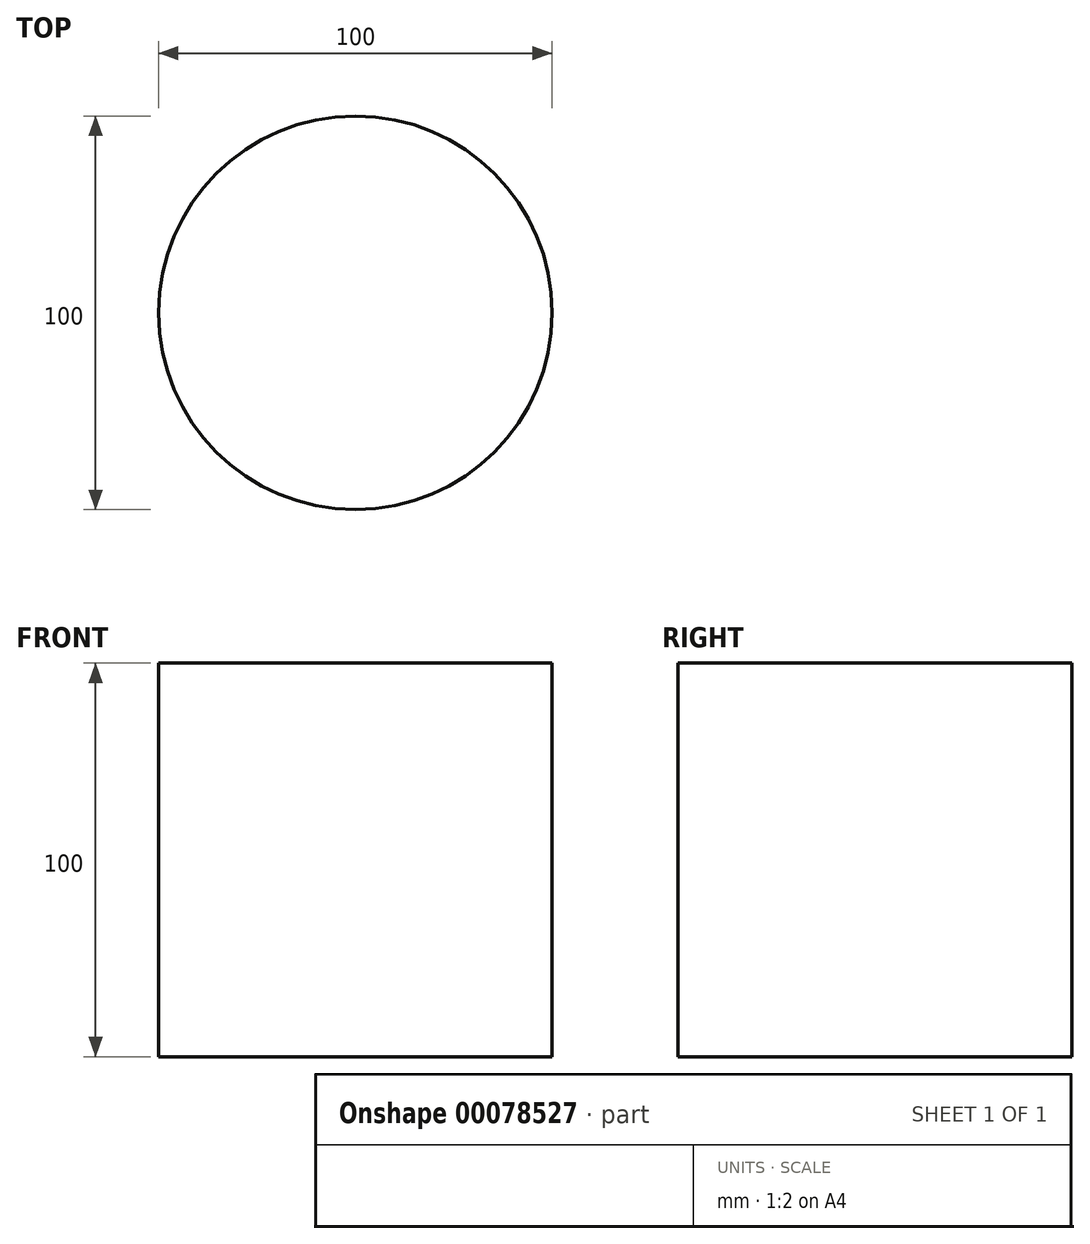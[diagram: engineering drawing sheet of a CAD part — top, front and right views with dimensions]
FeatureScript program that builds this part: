
annotation { "Feature Type Name" : "Feature", "Feature Type Description" : "" }
export const myFeature = defineFeature(function(context is Context, id is Id, definition is map)
    precondition{}
    {
        {
            var Q0;
            Q0=qCreatedBy(makeId("Front.planeOp"),FACE);
            var sketch = newSketch(context, id + "F0", { "sketchPlane" : qUnion([Q0])});
            skLineSegment(sketch, "E0.bottom", {"start": v(0, 100) * mm, "end": v(50, 100) * mm});
            skLineSegment(sketch, "E0.top", {"start": v(0, 0) * mm, "end": v(50, 0) * mm});
            skLineSegment(sketch, "E0.left", {"start": v(0, 100) * mm, "end": v(0, 0) * mm});
            skLineSegment(sketch, "E0.right", {"start": v(50, 100) * mm, "end": v(50, 0) * mm});
            skLineSegment(sketch, "E1", {"start": v(0, -9.88) * mm, "end": v(0, 125.5) * mm, "construction": true});
            skSolve(sketch);
        }
        {
            var Q0;
            Q0=makeQuery(id+"F0.imprint","IMPRINT",FACE,{"disambiguationData":[TD([[makeQuery(id+"F0.imprint","IMPRINT",EDGE,{"derivedFrom":sQuery(id+"F0.wireOp",EDGE,"E0.bottom")}),-1.0]])]});
            var Q1;
            Q1=sQuery(id+"F0.wireOp",EDGE,"E1");
            revolve(context, id + "F1", {"entities" : qUnion([Q0]), "axis" : qUnion([Q1]), "revolveType" : RevolveType.FULL});
        }
    });
